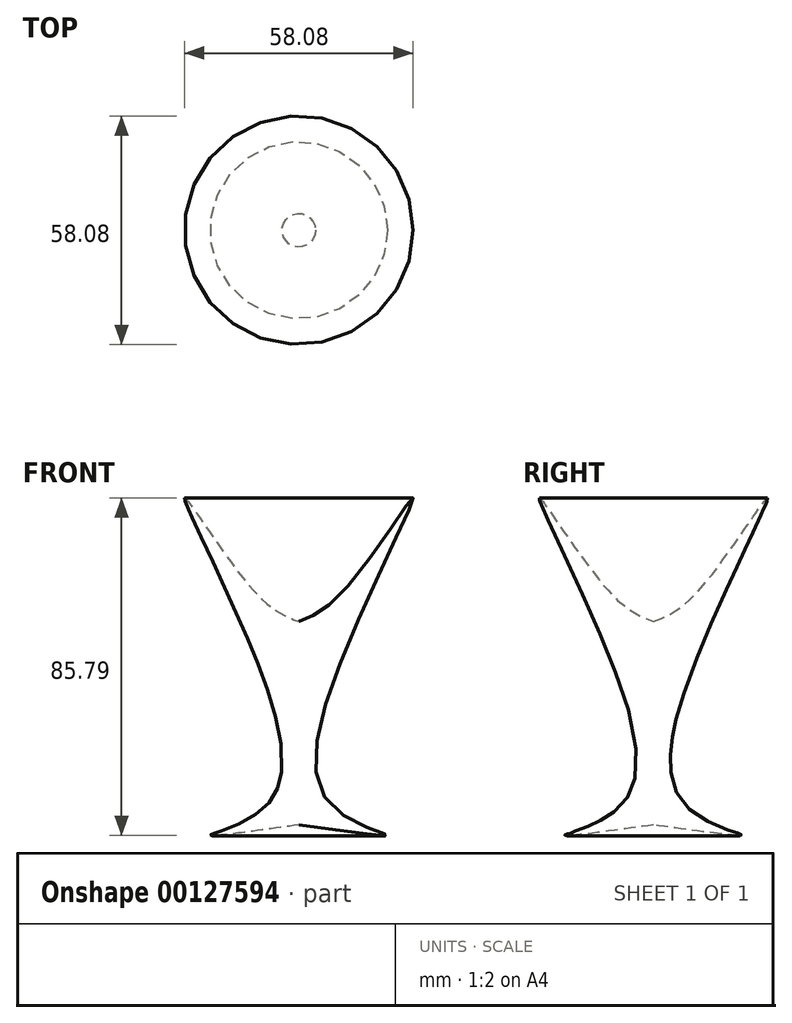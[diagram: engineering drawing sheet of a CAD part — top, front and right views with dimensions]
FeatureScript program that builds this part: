
annotation { "Feature Type Name" : "Feature", "Feature Type Description" : "" }
export const myFeature = defineFeature(function(context is Context, id is Id, definition is map)
    precondition{}
    {
        {
            var Q0;
            Q0=qCreatedBy(makeId("Front.planeOp"),FACE);
            var sketch = newSketch(context, id + "F0", { "sketchPlane" : qUnion([Q0])});
            skFitSpline(sketch, "E0", {"points": [v(0, -51.66) * mm, v(22.49, -54.23) * mm, v(8.3, -46.84) * mm, v(11.4, -8.32) * mm, v(28.94, 31.41) * mm, v(11.3, 7.68) * mm, v(0, 0) * mm], "startDerivative": vector(223.25, -31) * mm, "endDerivative": vector(-82.87, -32.01) * mm});
            skLineSegment(sketch, "E1", {"start": v(0, 0) * mm, "end": v(0, -51.66) * mm});
            skSolve(sketch);
        }
        {
            var Q0;
            Q0=makeQuery(id+"F0.imprint","IMPRINT",FACE,{"disambiguationData":[TD([[makeQuery(id+"F0.imprint","IMPRINT",EDGE,{"derivedFrom":sQuery(id+"F0.wireOp",EDGE,"E0")}),1.0]])]});
            var Q1;
            Q1=sQuery(id+"F0.wireOp",EDGE,"E1");
            revolve(context, id + "F1", {"entities" : qUnion([Q0]), "axis" : qUnion([Q1]), "revolveType" : RevolveType.FULL});
        }
    });
